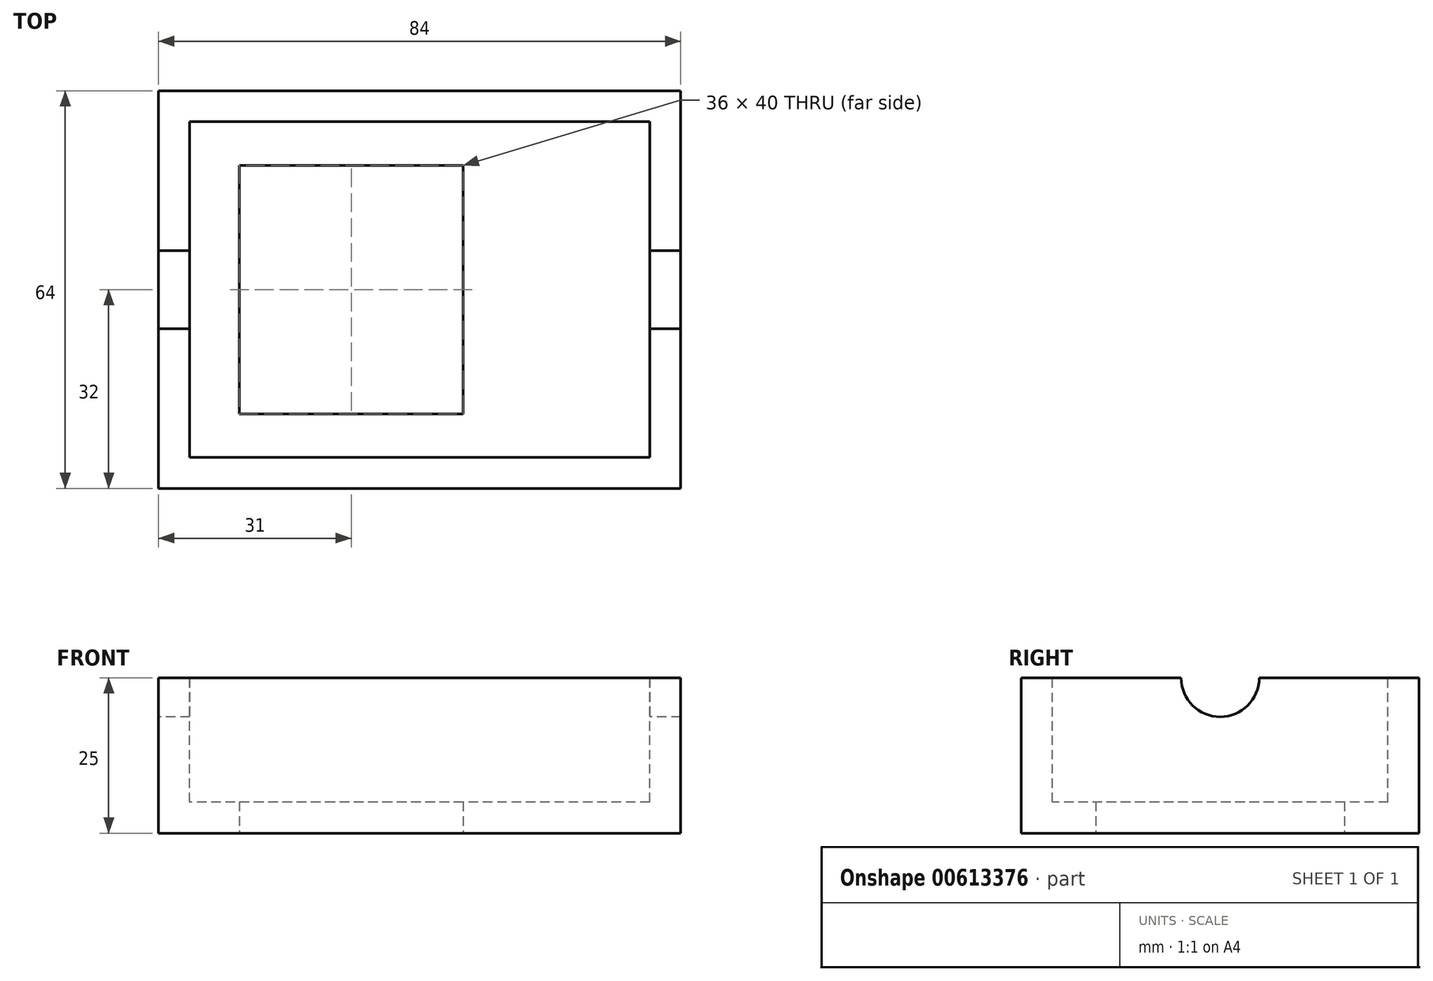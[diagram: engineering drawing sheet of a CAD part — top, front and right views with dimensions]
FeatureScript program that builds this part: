
annotation { "Feature Type Name" : "Feature", "Feature Type Description" : "" }
export const myFeature = defineFeature(function(context is Context, id is Id, definition is map)
    precondition{}
    {
        {
            var Q0;
            Q0=qCreatedBy(makeId("Top.planeOp"),FACE);
            var sketch = newSketch(context, id + "F0", { "sketchPlane" : qUnion([Q0])});
            skLineSegment(sketch, "E0.0", {"start": v(-54.59, 32) * mm, "end": v(-54.59, -32) * mm});
            skLineSegment(sketch, "E0.1", {"start": v(29.41, 32) * mm, "end": v(-54.59, 32) * mm});
            skLineSegment(sketch, "E0.2", {"start": v(29.41, 32) * mm, "end": v(29.41, -32) * mm});
            skLineSegment(sketch, "E0.3", {"start": v(29.41, -32) * mm, "end": v(-54.59, -32) * mm});
            skLineSegment(sketch, "E1.bottom", {"start": v(-5.59, 20) * mm, "end": v(-41.59, 20) * mm});
            skLineSegment(sketch, "E1.top", {"start": v(-5.59, -20) * mm, "end": v(-41.59, -20) * mm});
            skLineSegment(sketch, "E1.left", {"start": v(-5.59, 20) * mm, "end": v(-5.59, -20) * mm});
            skLineSegment(sketch, "E1.right", {"start": v(-41.59, 20) * mm, "end": v(-41.59, -20) * mm});
            skPoint(sketch, "E1.middle", {"position": v(-23.59, 0) * mm});
            skSolve(sketch);
        }
        {
            var Q0;
            Q0=qSketchRegion(id+"F0",true);
            extrude(context, id + "F1", {"entities" : qUnion([Q0]), "depth" : 25 * mm, "offsetDistance" : 25 * mm});
        }
        {
            var Q0;
            Q0=makeQuery(id+"F1.opExtrude","CAP_FACE",FACE,{"disambiguationData":[OSD([sQuery(id+"F0.wireOp",EDGE,"E0.0"),sQuery(id+"F0.wireOp",EDGE,"E0.1"),sQuery(id+"F0.wireOp",EDGE,"E0.2"),sQuery(id+"F0.wireOp",EDGE,"E0.3"),sQuery(id+"F0.wireOp",EDGE,"E1.bottom"),sQuery(id+"F0.wireOp",EDGE,"E1.top"),sQuery(id+"F0.wireOp",EDGE,"E1.left"),sQuery(id+"F0.wireOp",EDGE,"E1.right")])],"isStart":false});
            var sketch = newSketch(context, id + "F2", { "sketchPlane" : qUnion([Q0])});
            skLineSegment(sketch, "E2.0", {"start": v(-49.59, 27) * mm, "end": v(-49.59, -27) * mm});
            skLineSegment(sketch, "E2.1", {"start": v(24.41, 27) * mm, "end": v(-49.59, 27) * mm});
            skLineSegment(sketch, "E2.2", {"start": v(24.41, 27) * mm, "end": v(24.41, -27) * mm});
            skLineSegment(sketch, "E2.3", {"start": v(24.41, -27) * mm, "end": v(-49.59, -27) * mm});
            skSolve(sketch);
        }
        {
            var Q0;
            Q0=qSketchRegion(id+"F2",true);
            extrude(context, id + "F3", {"entities" : qUnion([Q0]), "operationType" : NewBodyOperationType.REMOVE, "oppositeDirection" : true, "depth" : 20 * mm, "offsetDistance" : 25 * mm});
        }
        {
            var Q0;
            Q0=makeQuery(id+"F1.opExtrude","SWEPT_FACE",FACE,{"disambiguationData":[OSD([sQuery(id+"F0.wireOp",EDGE,"E0.0")])]});
            var sketch = newSketch(context, id + "F4", { "sketchPlane" : qUnion([Q0])});
            skCircle(sketch, "E3", {"center": v(0, 25) * mm, "radius": 6.28 * mm});
            skSolve(sketch);
        }
        {
            var Q0;
            Q0=qSketchRegion(id+"F4",true);
            extrude(context, id + "F5", {"entities" : qUnion([Q0]), "operationType" : NewBodyOperationType.REMOVE, "oppositeDirection" : true, "depth" : 100 * mm, "offsetDistance" : 25 * mm});
        }
    });
